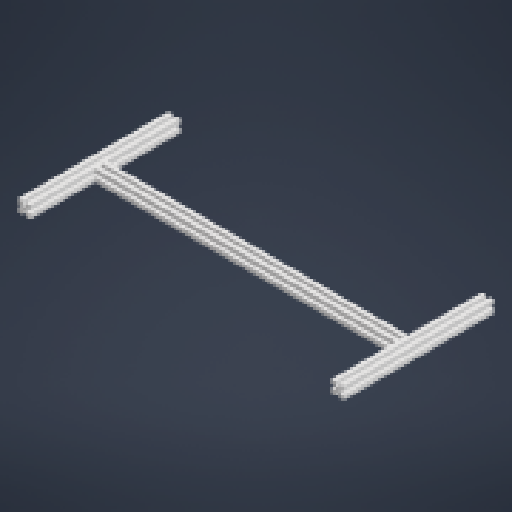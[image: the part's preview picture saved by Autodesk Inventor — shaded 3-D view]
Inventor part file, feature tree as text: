
AUTODESK INVENTOR PART (.ipt)
format: ipt  version: 2024 (Build 280153000, 153)  size: 479,744 bytes
history: native  units: mm
features: projected_geometry x12, extrude x6, sketch x6, reference x5, other x4
ambient origin geometry x8: Origin, YZ Plane, XZ Plane, XY Plane, X Axis, Y Axis, Z Axis, Center Point
bodies: Body1 (feature_tree)
feature tree (33):
  other  "솔리드1"
  extrude  "돌출1"  Depth=20.0mm
  extrude  "돌출2"  Depth=20.0mm
  extrude  "돌출3"  Depth=5.5mm
  extrude  "돌출4"  Depth=5.5mm
  extrude  "돌출5"  Depth=5.5mm
  extrude  "돌출6"  Depth=5.5mm
  sketch  "스케치1"
  reference  "참조1"
  sketch  "스케치2"
  projected_geometry  "투영된 루프1"
  projected_geometry  "투영된 루프2"
  sketch  "스케치3"
  projected_geometry  "투영된 루프3"
  projected_geometry  "투영된 루프4"
  reference  "참조2"
  reference  "참조3"
  sketch  "스케치4"
  projected_geometry  "투영된 루프5"
  projected_geometry  "투영된 루프6"
  projected_geometry  "투영된 루프7"
  projected_geometry  "투영된 루프8"
  projected_geometry  "투영된 루프9"
  reference  "참조4"
  reference  "참조5"
  sketch  "스케치5"
  projected_geometry  "투영된 루프10"
  projected_geometry  "투영된 루프11"
  sketch  "스케치6"
  projected_geometry  "투영된 루프12"
  other  "<userpath>\OneDrive\AAST\PART\ABCD\ABCD Assemble.iam"
  other  "ABCD Assemble.iam"
  other  "acrillboard:1"
